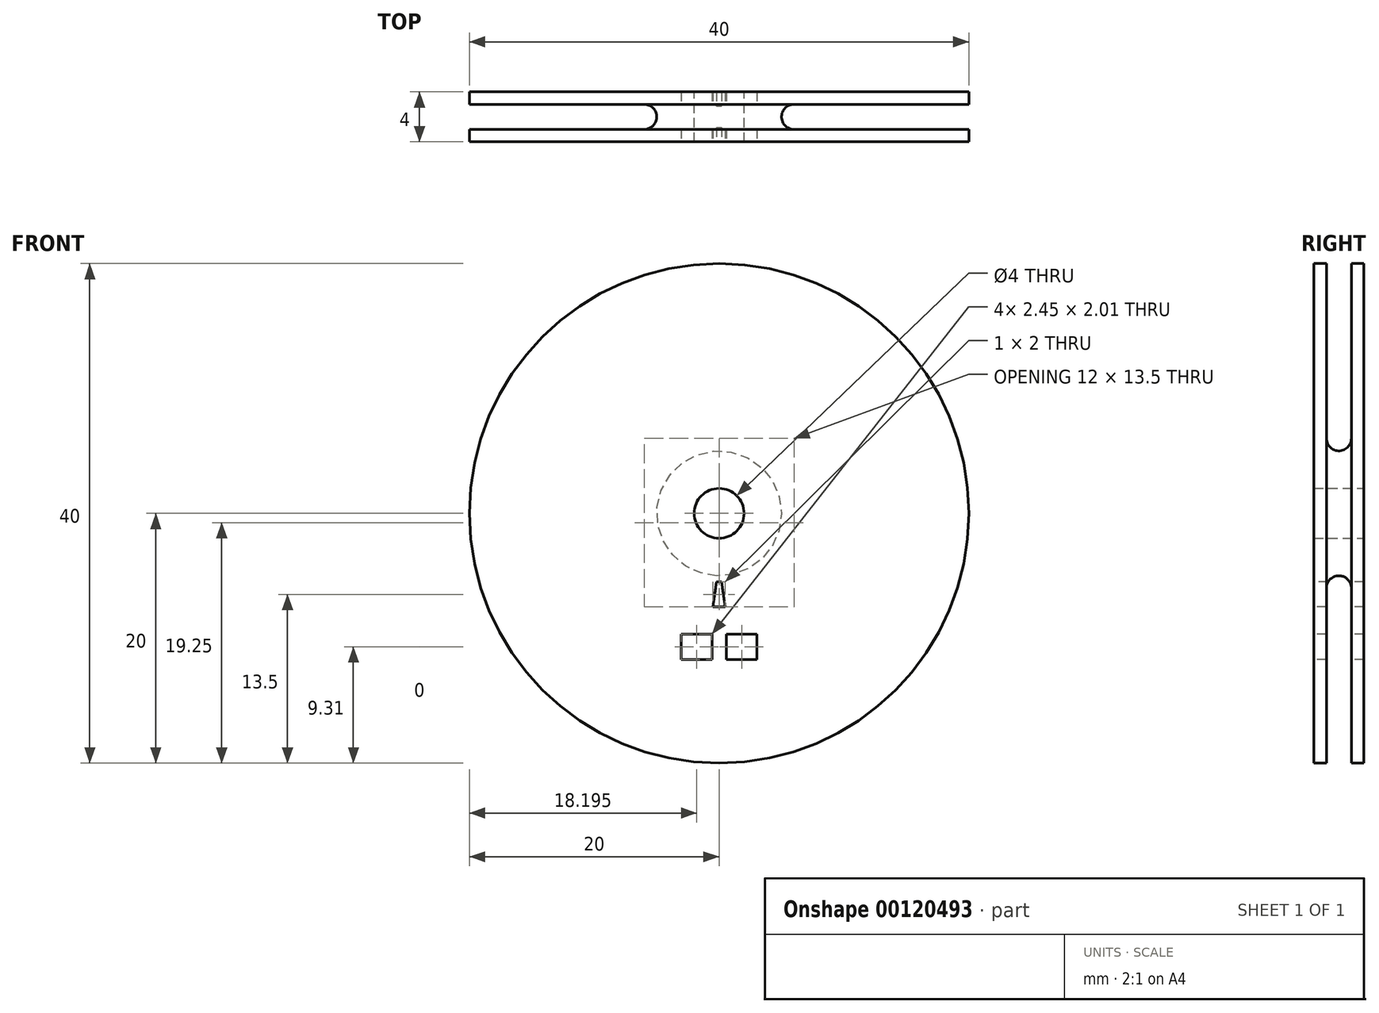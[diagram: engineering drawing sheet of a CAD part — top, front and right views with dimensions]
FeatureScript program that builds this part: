
annotation { "Feature Type Name" : "Feature", "Feature Type Description" : "" }
export const myFeature = defineFeature(function(context is Context, id is Id, definition is map)
    precondition{}
    {
        {
            var Q0;
            Q0=qCreatedBy(makeId("Front.planeOp"),FACE);
            var sketch = newSketch(context, id + "F0", { "sketchPlane" : qUnion([Q0])});
            skCircle(sketch, "E0", {"center": v(0, 0) * mm, "radius": 2 * mm});
            skCircle(sketch, "E1", {"center": v(0, 0) * mm, "radius": 20 * mm});
            skSolve(sketch);
        }
        {
            var Q0;
            Q0=makeQuery(id+"F0.imprint","IMPRINT",FACE,{"disambiguationData":[TD([[makeQuery(id+"F0.imprint","IMPRINT",EDGE,{"derivedFrom":sQuery(id+"F0.wireOp",EDGE,"E0")}),-1.0]])]});
            extrude(context, id + "F1", {"entities" : qUnion([Q0]), "depth" : 4 * mm, "symmetric" : true});
        }
        {
            var Q0;
            Q0=qCreatedBy(makeId("Right.planeOp"),FACE);
            var sketch = newSketch(context, id + "F2", { "sketchPlane" : qUnion([Q0])});
            skLineSegment(sketch, "E2", {"start": v(-2, 20) * mm, "end": v(-1, 20) * mm});
            skLineSegment(sketch, "E3", {"start": v(-1, 20) * mm, "end": v(-1, 6) * mm});
            skLineSegment(sketch, "E4", {"start": v(1, 20) * mm, "end": v(1, 6) * mm});
            skLineSegment(sketch, "E5", {"start": v(-1, 20) * mm, "end": v(1, 20) * mm});
            skLineSegment(sketch, "E6", {"start": v(1, 20) * mm, "end": v(2, 20) * mm});
            skCircle(sketch, "E7", {"center": v(0, 6) * mm, "radius": 1 * mm});
            skLineSegment(sketch, "E8", {"start": v(-2, 2) * mm, "end": v(2, 2) * mm});
            skLineSegment(sketch, "E9", {"start": v(0, 6) * mm, "end": v(0, 5) * mm});
            skSolve(sketch);
        }
        {
            var Q0;
            Q0 = qSketchRegion(id + "F2", true);
            var Q1;
            Q1=makeQuery(id+"F1.opExtrude","CAP_EDGE",EDGE,{"disambiguationData":[OSD([sQuery(id+"F0.wireOp",EDGE,"E0")])],"isStart":false});
            revolve(context, id + "F3", {"operationType" : NewBodyOperationType.REMOVE, "entities" : qUnion([Q0]), "axis" : qUnion([Q1]), "revolveType" : RevolveType.FULL, "oppositeDirection" : true});
        }
        {
            var Q0;
            Q0=makeQuery(id+"F1.opExtrude","CAP_FACE",FACE,{"disambiguationData":[OSD([sQuery(id+"F0.wireOp",EDGE,"E0"),sQuery(id+"F0.wireOp",EDGE,"E1")])],"isStart":false});
            var sketch = newSketch(context, id + "F4", { "sketchPlane" : qUnion([Q0])});
            skLineSegment(sketch, "E10.bottom", {"start": v(0, -5.5) * mm, "end": v(0.2, -5.5) * mm});
            skLineSegment(sketch, "E10.top", {"start": v(0, -7.5) * mm, "end": v(0.5, -7.5) * mm});
            skLineSegment(sketch, "E11.bottom", {"start": v(0, -5.5) * mm, "end": v(-0.2, -5.5) * mm});
            skLineSegment(sketch, "E11.top", {"start": v(0, -7.5) * mm, "end": v(-0.5, -7.5) * mm});
            skLineSegment(sketch, "E12.bottom", {"start": v(0, -9.69) * mm, "end": v(0.58, -9.69) * mm});
            skLineSegment(sketch, "E12.top", {"start": v(0, -11.7) * mm, "end": v(0.58, -11.7) * mm});
            skLineSegment(sketch, "E12.left", {"start": v(0, -9.69) * mm, "end": v(0, -11.7) * mm});
            skLineSegment(sketch, "E12.right", {"start": v(3.03, -9.69) * mm, "end": v(3.03, -11.7) * mm});
            skLineSegment(sketch, "E13.bottom", {"start": v(0, -11.7) * mm, "end": v(-0.58, -11.7) * mm});
            skLineSegment(sketch, "E13.top", {"start": v(0, -9.69) * mm, "end": v(-0.58, -9.69) * mm});
            skLineSegment(sketch, "E13.left", {"start": v(0, -11.7) * mm, "end": v(0, -9.69) * mm});
            skLineSegment(sketch, "E13.right", {"start": v(-3.03, -11.7) * mm, "end": v(-3.03, -9.69) * mm});
            skLineSegment(sketch, "E14.bottom", {"start": v(-0.58, -9.69) * mm, "end": v(0, -9.69) * mm});
            skLineSegment(sketch, "E14.top", {"start": v(-0.58, -11.7) * mm, "end": v(0, -11.7) * mm});
            skLineSegment(sketch, "E14.left", {"start": v(-0.58, -9.69) * mm, "end": v(-0.58, -11.7) * mm});
            skLineSegment(sketch, "E14.right", {"start": v(0.58, -9.69) * mm, "end": v(0.58, -11.7) * mm});
            skLineSegment(sketch, "E15", {"start": v(-0.58, -9.69) * mm, "end": v(-3.03, -9.69) * mm});
            skLineSegment(sketch, "E16", {"start": v(0.58, -9.69) * mm, "end": v(3.03, -9.69) * mm});
            skLineSegment(sketch, "E17", {"start": v(0.58, -11.7) * mm, "end": v(3.03, -11.7) * mm});
            skLineSegment(sketch, "E18", {"start": v(-0.58, -11.7) * mm, "end": v(-3.03, -11.7) * mm});
            skLineSegment(sketch, "E19", {"start": v(0.2, -5.5) * mm, "end": v(0.5, -7.5) * mm});
            skLineSegment(sketch, "E20", {"start": v(-0.2, -5.5) * mm, "end": v(-0.5, -7.5) * mm});
            skCircle(sketch, "E21.0", {"center": v(0, 0) * mm, "radius": 2 * mm});
            skSolve(sketch);
        }
        {
            var Q0;
            Q0=makeQuery(id+"F4.imprint","IMPRINT",FACE,{"disambiguationData":[TD([[makeQuery(id+"F4.imprint","IMPRINT",EDGE,{"derivedFrom":sQuery(id+"F4.wireOp",EDGE,"E13.right")}),-1.0]])]});
            var Q1;
            Q1=makeQuery(id+"F4.imprint","IMPRINT",FACE,{"disambiguationData":[TD([[makeQuery(id+"F4.imprint","IMPRINT",EDGE,{"derivedFrom":sQuery(id+"F4.wireOp",EDGE,"E12.right")}),-1.0]])]});
            extrude(context, id + "F5", {"entities" : qUnion([Q0, Q1]), "operationType" : NewBodyOperationType.REMOVE, "endBound" : BoundingType.THROUGH_ALL, "oppositeDirection" : true, "depth" : 25 * mm});
        }
        {
            var Q0;
            Q0=makeQuery(id+"F4.imprint","IMPRINT",FACE,{"disambiguationData":[TD([[makeQuery(id+"F4.imprint","IMPRINT",EDGE,{"derivedFrom":sQuery(id+"F4.wireOp",EDGE,"E10.bottom")}),-1.0]])]});
            extrude(context, id + "F6", {"entities" : qUnion([Q0]), "operationType" : NewBodyOperationType.REMOVE, "endBound" : BoundingType.THROUGH_ALL, "oppositeDirection" : true, "depth" : 25 * mm});
        }
    });
